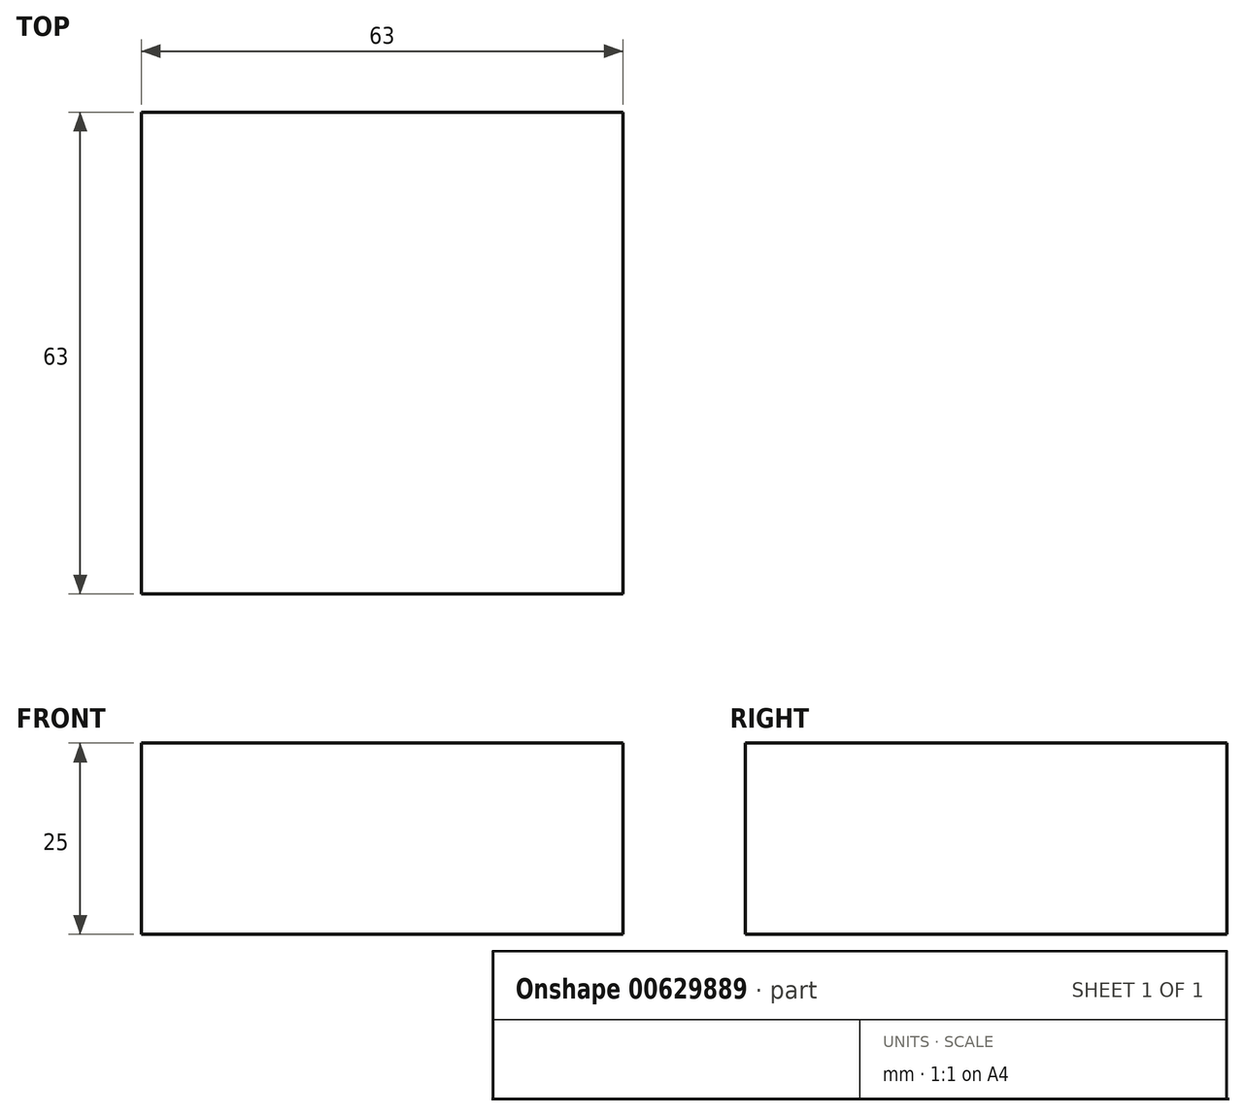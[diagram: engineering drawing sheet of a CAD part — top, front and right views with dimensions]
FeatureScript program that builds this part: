
annotation { "Feature Type Name" : "Feature", "Feature Type Description" : "" }
export const myFeature = defineFeature(function(context is Context, id is Id, definition is map)
    precondition{}
    {
        {
            var Q0;
            Q0=qCreatedBy(makeId("Top.planeOp"),FACE);
            var sketch = newSketch(context, id + "F0", { "sketchPlane" : qUnion([Q0])});
            skLineSegment(sketch, "E0.bottom", {"start": v(0, 0) * mm, "end": v(63, 0) * mm});
            skLineSegment(sketch, "E0.top", {"start": v(0, -63) * mm, "end": v(63, -63) * mm});
            skLineSegment(sketch, "E0.left", {"start": v(0, 0) * mm, "end": v(0, -63) * mm});
            skLineSegment(sketch, "E0.right", {"start": v(63, 0) * mm, "end": v(63, -63) * mm});
            skSolve(sketch);
        }
        {
            var Q0;
            Q0=makeQuery(id+"F0.imprint","IMPRINT",FACE,{"disambiguationData":[TD([[makeQuery(id+"F0.imprint","IMPRINT",EDGE,{"derivedFrom":sQuery(id+"F0.wireOp",EDGE,"E0.bottom")}),-1.0]])]});
            extrude(context, id + "F1", {"entities" : qUnion([Q0]), "depth" : 25 * mm, "offsetDistance" : 25 * mm});
        }
    });
